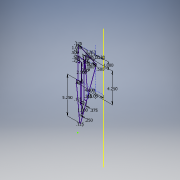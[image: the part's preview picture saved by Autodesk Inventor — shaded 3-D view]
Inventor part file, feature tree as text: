
AUTODESK INVENTOR PART (.ipt)
format: ipt  version: 2017 SP1 (Build 210196100, 196)  size: 132,608 bytes
history: native  units: in
note: dims shown in document units (in); Inventor stores cm internally (conversion verified against a paired STEP export)
features: sketch x1
ambient origin geometry x8: Origin, YZ Plane, XZ Plane, XY Plane, X Axis, Y Axis, Z Axis, Center Point
feature tree (1):
  sketch  "Sketch1"  dims[d0=1.13in d1=3.7625in d2=0.125in d3=0.1718in d5=1.0in d6=1.0in d7=90.0deg d8=0.5in d9=15.0deg d12=1.25in d13=0.25in d16=0.5in d17=0.5in d18=0.5in d19=2.5in d20=0.5in d22=0.375in d23=0.25in d25=0.234in d30=4.25in d31=0.25in d32=1.0in d33=0.8014in d34=15.0deg d36=0.125in d37=0.25in d39=4.0in d40=0.125in d41=5.25in d42=1.0in d43=0.125in]
